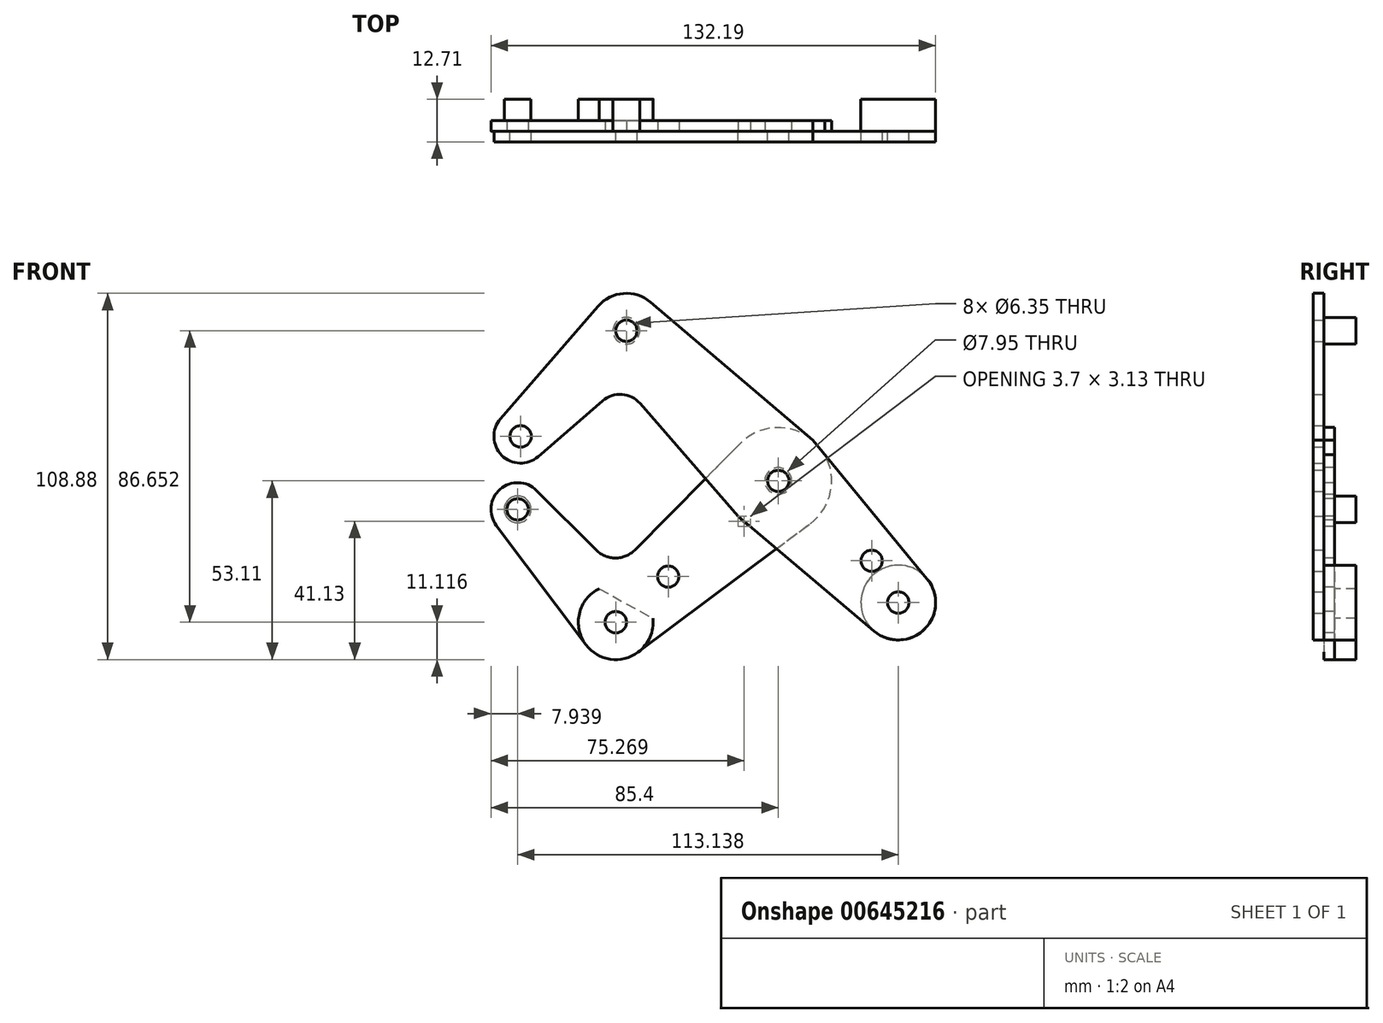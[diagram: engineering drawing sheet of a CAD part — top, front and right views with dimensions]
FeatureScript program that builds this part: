
annotation { "Feature Type Name" : "Feature", "Feature Type Description" : "" }
export const myFeature = defineFeature(function(context is Context, id is Id, definition is map)
    precondition{}
    {
        {
            var Q0;
            Q0=qCreatedBy(makeId("Front.planeOp"),FACE);
            var sketch = newSketch(context, id + "F0", { "sketchPlane" : qUnion([Q0])});
            skLineSegment(sketch, "E0", {"start": v(-76.57, 13.23) * mm, "end": v(-45.14, 44.66) * mm, "construction": true});
            skLineSegment(sketch, "E1", {"start": v(-45.14, 44.66) * mm, "end": v(35.68, -36.16) * mm, "construction": true});
            skCircle(sketch, "E2", {"center": v(-45.14, 44.66) * mm, "radius": 11.11 * mm});
            skCircle(sketch, "E3", {"center": v(-45.14, 44.66) * mm, "radius": 3.18 * mm});
            skCircle(sketch, "E4", {"center": v(0, 0) * mm, "radius": 15.88 * mm});
            skCircle(sketch, "E5", {"center": v(0, 0) * mm, "radius": 3.18 * mm});
            skCircle(sketch, "E6", {"center": v(0, 0) * mm, "radius": 3.98 * mm});
            skCircle(sketch, "E7", {"center": v(35.68, -36.16) * mm, "radius": 11.11 * mm});
            skCircle(sketch, "E8", {"center": v(35.68, -36.16) * mm, "radius": 3.18 * mm});
            skCircle(sketch, "E9", {"center": v(-76.57, 13.23) * mm, "radius": 7.94 * mm});
            skCircle(sketch, "E10", {"center": v(-76.57, 13.23) * mm, "radius": 3.18 * mm});
            skCircle(sketch, "E11", {"center": v(27.75, -23.75) * mm, "radius": 3.18 * mm});
            skLineSegment(sketch, "E12", {"start": v(-71.38, 7.23) * mm, "end": v(-52.25, 23.8) * mm});
            skLineSegment(sketch, "E13", {"start": v(-82.57, 18.42) * mm, "end": v(-53.54, 51.93) * mm});
            skLineSegment(sketch, "E14", {"start": v(-37.94, 53.12) * mm, "end": v(10.29, 12.1) * mm});
            skLineSegment(sketch, "E15", {"start": v(-53.53, 37.37) * mm, "end": v(-53.02, 36.78) * mm});
            skLineSegment(sketch, "E16", {"start": v(10.29, 12.1) * mm, "end": v(44.25, -29.1) * mm});
            skLineSegment(sketch, "E17", {"start": v(-11.98, -10.42) * mm, "end": v(28.5, -44.65) * mm});
            skLineSegment(sketch, "E18", {"start": v(0, 0) * mm, "end": v(-48.3, -42) * mm, "construction": true});
            skLineSegment(sketch, "E19", {"start": v(-48.3, -42) * mm, "end": v(-77.46, -8.45) * mm, "construction": true});
            skLineSegment(sketch, "E20.trimOffspring", {"start": v(-41.04, 23) * mm, "end": v(-11.98, -10.42) * mm});
            skPoint(sketch, "E21.visualSharp", {"position": v(-46.25, 29) * mm});
            skArc(sketch, "E21.filletArc", {"start": v(-41.04, 23) * mm, "mid": v(-46.48, 25.72) * mm, "end": v(-52.25, 23.8) * mm});
            skCircle(sketch, "E22", {"center": v(-77.46, -8.45) * mm, "radius": 7.94 * mm});
            skCircle(sketch, "E23", {"center": v(-77.46, -8.45) * mm, "radius": 3.18 * mm});
            skCircle(sketch, "E24", {"center": v(-48.3, -42) * mm, "radius": 11.11 * mm});
            skCircle(sketch, "E25", {"center": v(-48.3, -42) * mm, "radius": 3.18 * mm});
            skCircle(sketch, "E26", {"center": v(-32.71, -28.44) * mm, "radius": 3.18 * mm});
            skLineSegment(sketch, "E27", {"start": v(-83.8, -13.22) * mm, "end": v(-57.18, -48.67) * mm});
            skLineSegment(sketch, "E28", {"start": v(-71.86, -2.83) * mm, "end": v(-54, -20.63) * mm});
            skLineSegment(sketch, "E29", {"start": v(-41.65, -50.9) * mm, "end": v(9.5, -12.72) * mm});
            skLineSegment(sketch, "E30", {"start": v(-56.19, -34.17) * mm, "end": v(-55.6, -33.59) * mm});
            skLineSegment(sketch, "E31.trimOffspring", {"start": v(-42.74, -20.59) * mm, "end": v(-11.28, 11.17) * mm});
            skPoint(sketch, "E32.visualSharp", {"position": v(-48.35, -26.26) * mm});
            skArc(sketch, "E32.filletArc", {"start": v(-54, -20.63) * mm, "mid": v(-48.36, -22.95) * mm, "end": v(-42.74, -20.59) * mm});
            skSolve(sketch);
        }
        {
            var Q0;
            {var subQ4=sQuery(id+"F0.wireOp",EDGE,"E12");Q0=makeQuery(id+"F0.imprint","IMPRINT",FACE,{"disambiguationData":[TD([[makeQuery(id+"F0.imprint","IMPRINT",EDGE,{"derivedFrom":subQ4}),1.0]])]});}
            var Q1;
            Q1=makeQuery(id+"F0.imprint","IMPRINT",FACE,{"disambiguationData":[TD([[makeQuery(id+"F0.imprint","IMPRINT",EDGE,{"derivedFrom":sQuery(id+"F0.wireOp",EDGE,"E10")}),-1.0]])]});
            var Q2;
            Q2=makeQuery(id+"F0.imprint","IMPRINT",FACE,{"disambiguationData":[TD([[makeQuery(id+"F0.imprint","IMPRINT",EDGE,{"derivedFrom":sQuery(id+"F0.wireOp",EDGE,"E3")}),-1.0]])]});
            var Q3;
            Q3=makeQuery(id+"F0.imprint","IMPRINT",FACE,{"disambiguationData":[TD([[makeQuery(id+"F0.imprint","IMPRINT",EDGE,{"derivedFrom":sQuery(id+"F0.wireOp",EDGE,"E6")}),-1.0]])]});
            var Q4;
            Q4=makeQuery(id+"F0.imprint","IMPRINT",FACE,{"disambiguationData":[TD([[makeQuery(id+"F0.imprint","IMPRINT",EDGE,{"derivedFrom":sQuery(id+"F0.wireOp",EDGE,"E11")}),-1.0]])]});
            var Q5;
            Q5=makeQuery(id+"F0.imprint","IMPRINT",FACE,{"disambiguationData":[TD([[makeQuery(id+"F0.imprint","IMPRINT",EDGE,{"derivedFrom":sQuery(id+"F0.wireOp",EDGE,"E8")}),-1.0]])]});
            var Q6;
            Q6=makeQuery(id+"F0.imprint","IMPRINT",FACE,{"disambiguationData":[TD([[makeQuery(id+"F0.imprint","IMPRINT",EDGE,{"derivedFrom":sQuery(id+"F0.wireOp",EDGE,"E5")}),-1.0]])]});
            var Q7;
            {var subQ0=sQuery(id+"F0.wireOp",EDGE,"E29");var subQ1=sQuery(id+"F0.wireOp",EDGE,"E4");var subQ2=makeQuery(id+"F0.imprint","INTERSECT",VERTEX,{"derivedFrom":[subQ1,subQ0]});Q7=makeQuery(id+"F0.imprint","IMPRINT",FACE,{"disambiguationData":[TD([[makeQuery(id+"F0.imprint","IMPRINT",EDGE,{"disambiguationData":[TD([[subQ2,1.0]])],"derivedFrom":subQ1}),-1.0]])]});}
            var Q8;
            {var subQ1=sQuery(id+"F0.wireOp",EDGE,"E4");var subQ3=sQuery(id+"F0.wireOp",EDGE,"E31.trimOffspring");var subQ4=makeQuery(id+"F0.imprint","INTERSECT",VERTEX,{"derivedFrom":[subQ1,subQ3]});Q8=makeQuery(id+"F0.imprint","IMPRINT",FACE,{"disambiguationData":[TD([[makeQuery(id+"F0.imprint","IMPRINT",EDGE,{"disambiguationData":[TD([[subQ4,1.0]])],"derivedFrom":subQ3}),-1.0]])]});}
            extrude(context, id + "F1", {"entities" : qUnion([Q0, Q1, Q2, Q3, Q4, Q5, Q6, Q7, Q8]), "depth" : 3.17 * mm, "offsetDistance" : 25.4 * mm});
        }
        {
            var Q0;
            Q0=makeQuery(id+"F0.imprint","IMPRINT",FACE,{"disambiguationData":[TD([[makeQuery(id+"F0.imprint","IMPRINT",EDGE,{"derivedFrom":sQuery(id+"F0.wireOp",EDGE,"E23")}),-1.0]])]});
            var Q1;
            Q1=makeQuery(id+"F0.imprint","IMPRINT",FACE,{"disambiguationData":[TD([[makeQuery(id+"F0.imprint","IMPRINT",EDGE,{"derivedFrom":sQuery(id+"F0.wireOp",EDGE,"E26")}),-1.0]])]});
            var Q2;
            Q2=makeQuery(id+"F0.imprint","IMPRINT",FACE,{"disambiguationData":[TD([[makeQuery(id+"F0.imprint","IMPRINT",EDGE,{"derivedFrom":sQuery(id+"F0.wireOp",EDGE,"E25")}),-1.0]])]});
            var Q3;
            Q3=makeQuery(id+"F0.imprint","IMPRINT",FACE,{"disambiguationData":[TD([[makeQuery(id+"F0.imprint","IMPRINT",EDGE,{"derivedFrom":sQuery(id+"F0.wireOp",EDGE,"E6")}),-1.0]])]});
            var Q4;
            {var subQ0=sQuery(id+"F0.wireOp",EDGE,"E29");var subQ1=sQuery(id+"F0.wireOp",EDGE,"E4");var subQ2=makeQuery(id+"F0.imprint","INTERSECT",VERTEX,{"derivedFrom":[subQ1,subQ0]});Q4=makeQuery(id+"F0.imprint","IMPRINT",FACE,{"disambiguationData":[TD([[makeQuery(id+"F0.imprint","IMPRINT",EDGE,{"disambiguationData":[TD([[subQ2,1.0]])],"derivedFrom":subQ1}),-1.0]])]});}
            var Q5;
            {var subQ1=sQuery(id+"F0.wireOp",EDGE,"E4");var subQ3=sQuery(id+"F0.wireOp",EDGE,"E31.trimOffspring");var subQ4=makeQuery(id+"F0.imprint","INTERSECT",VERTEX,{"derivedFrom":[subQ1,subQ3]});Q5=makeQuery(id+"F0.imprint","IMPRINT",FACE,{"disambiguationData":[TD([[makeQuery(id+"F0.imprint","IMPRINT",EDGE,{"disambiguationData":[TD([[subQ4,1.0]])],"derivedFrom":subQ3}),-1.0]])]});}
            extrude(context, id + "F2", {"entities" : qUnion([Q0, Q1, Q2, Q3, Q4, Q5]), "oppositeDirection" : true, "depth" : 3.17 * mm, "offsetDistance" : 25.4 * mm});
        }
        {
            var Q0;
            Q0=makeQuery(id+"F1.opExtrude","CAP_FACE",FACE,{"disambiguationData":[OSD([sQuery(id+"F0.wireOp",EDGE,"E2"),sQuery(id+"F0.wireOp",EDGE,"E3"),sQuery(id+"F0.wireOp",EDGE,"E5"),sQuery(id+"F0.wireOp",EDGE,"E7"),sQuery(id+"F0.wireOp",EDGE,"E8"),sQuery(id+"F0.wireOp",EDGE,"E9"),sQuery(id+"F0.wireOp",EDGE,"E10"),sQuery(id+"F0.wireOp",EDGE,"E11"),sQuery(id+"F0.wireOp",EDGE,"E12"),sQuery(id+"F0.wireOp",EDGE,"E13"),sQuery(id+"F0.wireOp",EDGE,"E14"),sQuery(id+"F0.wireOp",EDGE,"E16"),sQuery(id+"F0.wireOp",EDGE,"E17"),sQuery(id+"F0.wireOp",EDGE,"E20.trimOffspring"),sQuery(id+"F0.wireOp",EDGE,"E21.filletArc")])],"isStart":false});
            var sketch = newSketch(context, id + "F3", { "sketchPlane" : qUnion([Q0])});
            skCircle(sketch, "E33", {"center": v(-45.14, 44.66) * mm, "radius": 3.98 * mm});
            skCircle(sketch, "E34.0", {"center": v(35.68, -36.16) * mm, "radius": 11.11 * mm});
            skSolve(sketch);
        }
        {
            var Q0;
            Q0=makeQuery(id+"F2.opExtrude","CAP_FACE",FACE,{"disambiguationData":[OSD([sQuery(id+"F0.wireOp",EDGE,"E4"),sQuery(id+"F0.wireOp",EDGE,"E6"),sQuery(id+"F0.wireOp",EDGE,"E16"),sQuery(id+"F0.wireOp",EDGE,"E17"),sQuery(id+"F0.wireOp",EDGE,"E22"),sQuery(id+"F0.wireOp",EDGE,"E23"),sQuery(id+"F0.wireOp",EDGE,"E24"),sQuery(id+"F0.wireOp",EDGE,"E25"),sQuery(id+"F0.wireOp",EDGE,"E26"),sQuery(id+"F0.wireOp",EDGE,"E27"),sQuery(id+"F0.wireOp",EDGE,"E28"),sQuery(id+"F0.wireOp",EDGE,"E29"),sQuery(id+"F0.wireOp",EDGE,"E31.trimOffspring"),sQuery(id+"F0.wireOp",EDGE,"E32.filletArc")])],"isStart":false});
            var sketch = newSketch(context, id + "F4", { "sketchPlane" : qUnion([Q0])});
            skCircle(sketch, "E35", {"center": v(77.46, -8.45) * mm, "radius": 3.98 * mm});
            skLineSegment(sketch, "E36", {"start": v(48.3, -42) * mm, "end": v(7.71, 31.63) * mm, "construction": true});
            skLineSegment(sketch, "E37", {"start": v(37.24, -40.83) * mm, "end": v(53.22, -32.03) * mm});
            skArc(sketch, "E38.0", {"start": v(53.22, -32.03) * mm, "mid": v(53.66, -51.73) * mm, "end": v(37.24, -40.83) * mm});
            skSolve(sketch);
        }
        {
            var Q0;
            Q0=qCreatedBy(makeId("Front.planeOp"),FACE);
            cPlane(context, id + "F5", {"entities" : qUnion([Q0]), "cplaneType" : CPlaneType.OFFSET, "offset" : 9.52 * mm, "oppositeDirection" : true, "width" : 152.4 * mm, "height" : 152.4 * mm});
        }
        {
            var Q0;
            Q0 = qSketchRegion(id + "F3", true);
            var Q1;
            Q1 = qSketchRegion(id + "F4", true);
            var Q2;
            Q2=qCreatedBy(id+"F5.planeOp",FACE);
            extrude(context, id + "F6", {"entities" : qUnion([Q0, Q1]), "endBound" : BoundingType.UP_TO_SURFACE, "oppositeDirection" : true, "depth" : 25.4 * mm, "endBoundEntityFace" : qUnion([Q2]), "offsetDistance" : 25.4 * mm});
        }
        {
            var Q0;
            Q0=makeQuery(id+"F1.opExtrude","SWEPT_BODY",BODY,{"disambiguationData":[OSD([sQuery(id+"F0.wireOp",EDGE,"E2"),sQuery(id+"F0.wireOp",EDGE,"E3"),sQuery(id+"F0.wireOp",EDGE,"E5"),sQuery(id+"F0.wireOp",EDGE,"E7"),sQuery(id+"F0.wireOp",EDGE,"E8"),sQuery(id+"F0.wireOp",EDGE,"E9"),sQuery(id+"F0.wireOp",EDGE,"E10"),sQuery(id+"F0.wireOp",EDGE,"E11"),sQuery(id+"F0.wireOp",EDGE,"E12"),sQuery(id+"F0.wireOp",EDGE,"E13"),sQuery(id+"F0.wireOp",EDGE,"E14"),sQuery(id+"F0.wireOp",EDGE,"E16"),sQuery(id+"F0.wireOp",EDGE,"E17"),sQuery(id+"F0.wireOp",EDGE,"E20.trimOffspring"),sQuery(id+"F0.wireOp",EDGE,"E21.filletArc")])]});
            var Q1;
            Q1=makeQuery(id+"F2.opExtrude","SWEPT_BODY",BODY,{"disambiguationData":[OSD([sQuery(id+"F0.wireOp",EDGE,"E4"),sQuery(id+"F0.wireOp",EDGE,"E6"),sQuery(id+"F0.wireOp",EDGE,"E16"),sQuery(id+"F0.wireOp",EDGE,"E17"),sQuery(id+"F0.wireOp",EDGE,"E22"),sQuery(id+"F0.wireOp",EDGE,"E23"),sQuery(id+"F0.wireOp",EDGE,"E24"),sQuery(id+"F0.wireOp",EDGE,"E25"),sQuery(id+"F0.wireOp",EDGE,"E26"),sQuery(id+"F0.wireOp",EDGE,"E27"),sQuery(id+"F0.wireOp",EDGE,"E28"),sQuery(id+"F0.wireOp",EDGE,"E29"),sQuery(id+"F0.wireOp",EDGE,"E31.trimOffspring"),sQuery(id+"F0.wireOp",EDGE,"E32.filletArc")])]});
            var Q2;
            Q2=makeQuery(id+"F6.opExtrude","SWEPT_BODY",BODY,{"disambiguationData":[OSD([sQuery(id+"F3.wireOp",EDGE,"E34.0")])]});
            var Q3;
            Q3=makeQuery(id+"F6.opExtrude","SWEPT_BODY",BODY,{"disambiguationData":[OSD([sQuery(id+"F3.wireOp",EDGE,"E33")])]});
            var Q4;
            Q4=makeQuery(id+"F6.opExtrude","SWEPT_BODY",BODY,{"disambiguationData":[OSD([sQuery(id+"F4.wireOp",EDGE,"E35")])]});
            var Q5;
            Q5=makeQuery(id+"F6.opExtrude","SWEPT_BODY",BODY,{"disambiguationData":[OSD([sQuery(id+"F4.wireOp",EDGE,"E37"),sQuery(id+"F4.wireOp",EDGE,"E38.0")])]});
            booleanBodies(context, id + "F7", {"operationType" : BooleanOperationType.SUBTRACTION, "tools" : qUnion([Q0, Q1]), "targets" : qUnion([Q2, Q3, Q4, Q5]), "keepTools" : true});
        }
    });
